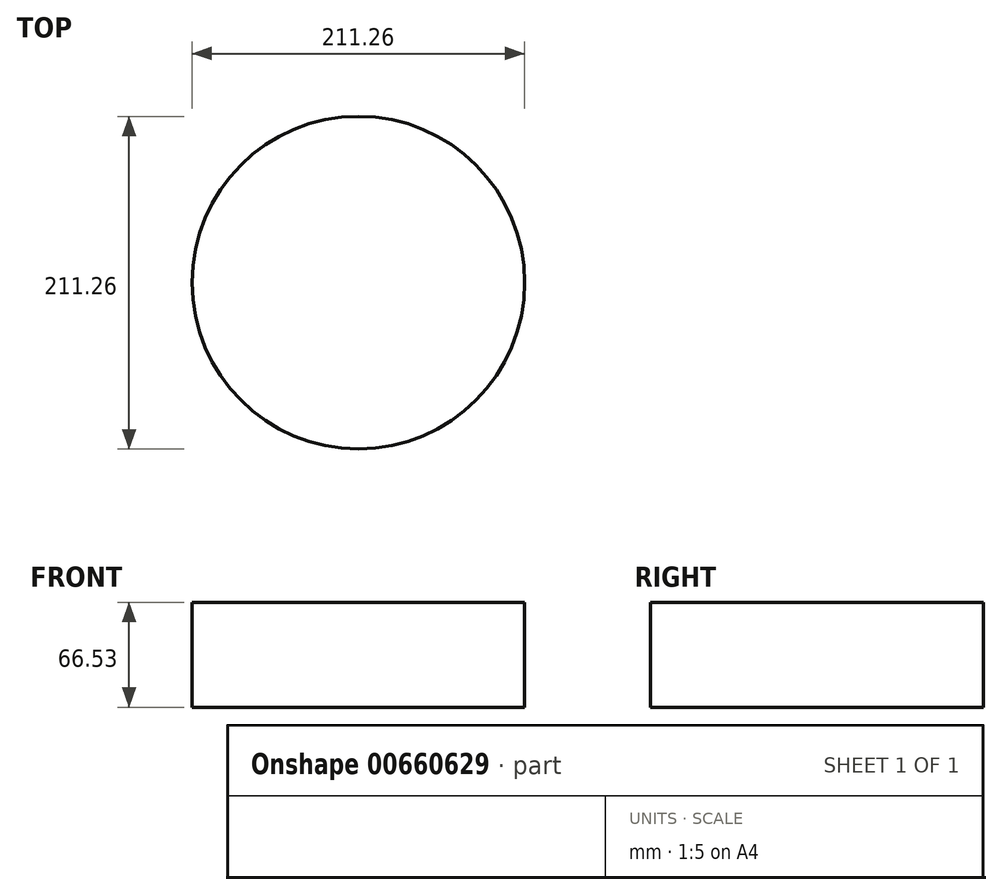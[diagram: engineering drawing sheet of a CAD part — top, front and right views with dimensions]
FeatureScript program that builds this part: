
annotation { "Feature Type Name" : "Feature", "Feature Type Description" : "" }
export const myFeature = defineFeature(function(context is Context, id is Id, definition is map)
    precondition{}
    {
        {
            var Q0;
            Q0=qCreatedBy(makeId("Top.planeOp"),FACE);
            var sketch = newSketch(context, id + "F0", { "sketchPlane" : qUnion([Q0])});
            skCircle(sketch, "E0", {"center": v(0, 0) * mm, "radius": 127 * mm});
            skSolve(sketch);
        }
        {
            var Q0;
            Q0=makeQuery(id+"F0.imprint","IMPRINT",FACE,{"disambiguationData":[TD([[makeQuery(id+"F0.imprint","IMPRINT",EDGE,{"derivedFrom":sQuery(id+"F0.wireOp",EDGE,"E0")}),1.0]])]});
            extrude(context, id + "F1", {"entities" : qUnion([Q0]), "depth" : 80 * mm, "offsetDistance" : 25.4 * mm});
        }
        {
            var Q0;
            Q0=makeQuery(id+"F1.opExtrude","CAP_FACE",FACE,{"disambiguationData":[OSD([sQuery(id+"F0.wireOp",EDGE,"E0")])],"isStart":false});
            var sketch = newSketch(context, id + "F2", { "sketchPlane" : qUnion([Q0])});
            skCircle(sketch, "E1", {"center": v(0, 0) * mm, "radius": 105.69 * mm});
            skSolve(sketch);
        }
        {
            var Q0;
            Q0=makeQuery(id+"F2.imprint","IMPRINT",FACE,{"disambiguationData":[TD([[makeQuery(id+"F2.imprint","IMPRINT",EDGE,{"derivedFrom":sQuery(id+"F2.wireOp",EDGE,"E1")}),1.0]])]});
            extrude(context, id + "F3", {"entities" : qUnion([Q0]), "operationType" : NewBodyOperationType.REMOVE, "oppositeDirection" : true, "depth" : 69.6 * mm, "offsetDistance" : 25.4 * mm});
        }
        {
            var Q0;
            Q0=makeQuery(id+"F3.boolean.opBoolean","COPY",FACE,{"derivedFrom":makeQuery(id+"F3.opExtrude","CAP_FACE",FACE,{"disambiguationData":[OSD([sQuery(id+"F2.wireOp",EDGE,"E1")])],"isStart":false})});
            var sketch = newSketch(context, id + "F4", { "sketchPlane" : qUnion([Q0])});
            skCircle(sketch, "E2", {"center": v(0, 0) * mm, "radius": 105.63 * mm});
            skSolve(sketch);
        }
        {
            var Q0;
            Q0=makeQuery(id+"F4.imprint","IMPRINT",FACE,{"disambiguationData":[TD([[makeQuery(id+"F4.imprint","IMPRINT",EDGE,{"derivedFrom":sQuery(id+"F4.wireOp",EDGE,"E2")}),1.0]])]});
            extrude(context, id + "F5", {"entities" : qUnion([Q0]), "operationType" : NewBodyOperationType.ADD, "depth" : 67.3 * mm, "offsetDistance" : 25.4 * mm});
        }
        {
            var Q0;
            Q0=makeQuery(id+"F1.opExtrude","CAP_FACE",FACE,{"disambiguationData":[OSD([sQuery(id+"F0.wireOp",EDGE,"E0")])],"isStart":false});
            var sketch = newSketch(context, id + "F6", { "sketchPlane" : qUnion([Q0])});
            skCircle(sketch, "E3.0.0", {"center": v(0, 0) * mm, "radius": 127 * mm});
            skSolve(sketch);
        }
        {
            var Q0;
            Q0=makeQuery(id+"F6.imprint","IMPRINT",FACE,{"disambiguationData":[TD([[makeQuery(id+"F6.imprint","IMPRINT",EDGE,{"derivedFrom":sQuery(id+"F6.wireOp",EDGE,"E3.0.0")}),1.0]])]});
            extrude(context, id + "F7", {"entities" : qUnion([Q0]), "operationType" : NewBodyOperationType.REMOVE, "oppositeDirection" : true, "depth" : 109.47 * mm, "offsetDistance" : 25.4 * mm});
        }
        {
            var Q0;
            Q0=makeQuery(id+"F1.opExtrude","CAP_FACE",FACE,{"disambiguationData":[OSD([sQuery(id+"F0.wireOp",EDGE,"E0")])],"isStart":true});
            var sketch = newSketch(context, id + "F8", { "sketchPlane" : qUnion([Q0])});
            skCircle(sketch, "E4.0.0", {"center": v(0, 0) * mm, "radius": 105.69 * mm});
            skSolve(sketch);
        }
        {
            var Q0;
            Q0=makeQuery(id+"F8.imprint","IMPRINT",FACE,{"disambiguationData":[TD([[makeQuery(id+"F8.imprint","IMPRINT",EDGE,{"derivedFrom":sQuery(id+"F8.wireOp",EDGE,"E4.0.0")}),-1.0]])]});
            extrude(context, id + "F9", {"entities" : qUnion([Q0]), "operationType" : NewBodyOperationType.REMOVE, "oppositeDirection" : true, "depth" : 11.18 * mm, "offsetDistance" : 25.4 * mm});
        }
    });
